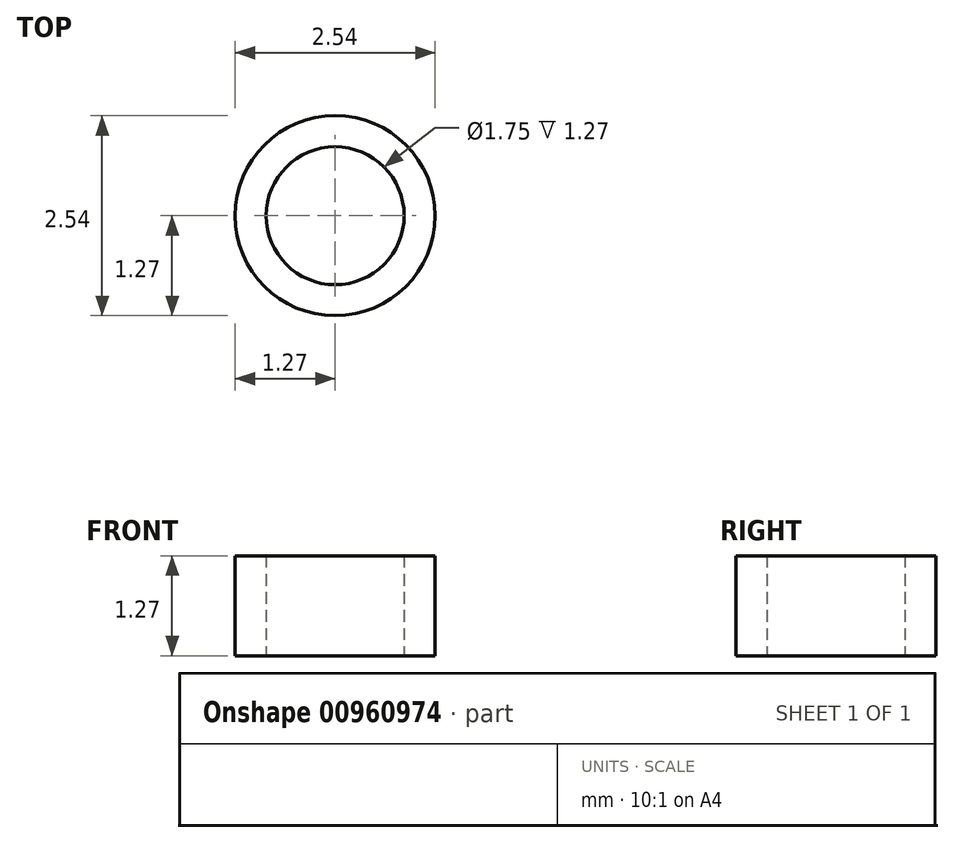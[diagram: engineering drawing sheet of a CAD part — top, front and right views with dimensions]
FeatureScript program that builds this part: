
annotation { "Feature Type Name" : "Feature", "Feature Type Description" : "" }
export const myFeature = defineFeature(function(context is Context, id is Id, definition is map)
    precondition{}
    {
        {
            var Q0;
            Q0=qCreatedBy(makeId("Top.planeOp"),FACE);
            var sketch = newSketch(context, id + "F0", { "sketchPlane" : qUnion([Q0])});
            skCircle(sketch, "E0", {"center": v(0, 0) * mm, "radius": 0.88 * mm});
            skCircle(sketch, "E1", {"center": v(0, 0) * mm, "radius": 1.27 * mm});
            skSolve(sketch);
        }
        {
            var Q0;
            Q0=makeQuery(id+"F0.imprint","IMPRINT",FACE,{"disambiguationData":[TD([[makeQuery(id+"F0.imprint","IMPRINT",EDGE,{"derivedFrom":sQuery(id+"F0.wireOp",EDGE,"E0")}),-1.0]])]});
            extrude(context, id + "F1", {"entities" : qUnion([Q0]), "depth" : 1.27 * mm, "offsetDistance" : 25.4 * mm});
        }
    });
